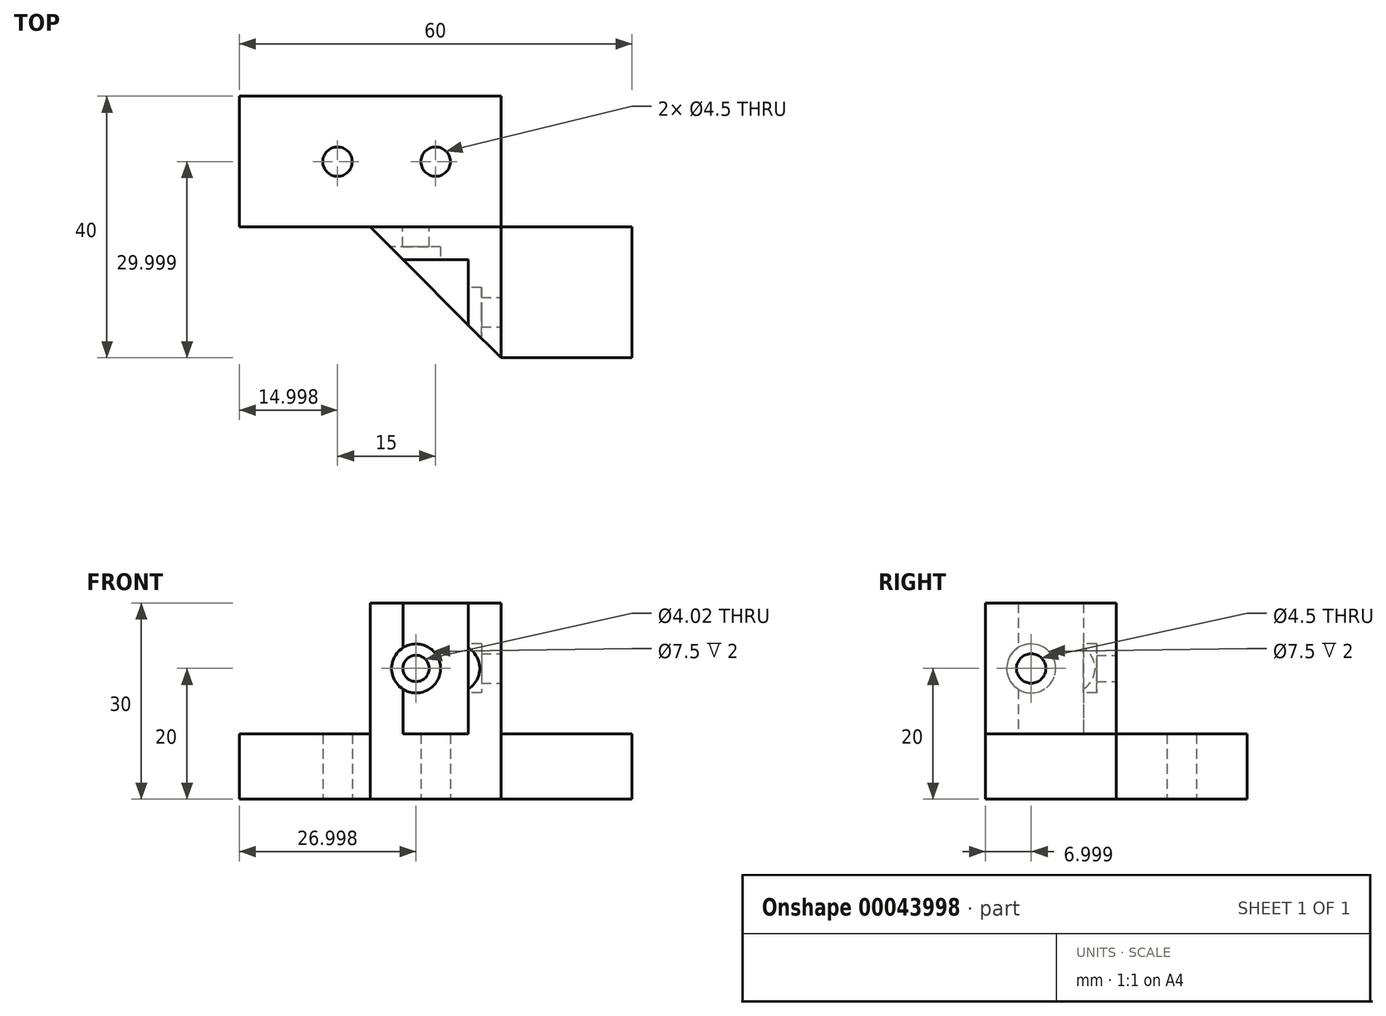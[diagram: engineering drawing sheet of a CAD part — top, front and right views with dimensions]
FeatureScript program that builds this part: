
annotation { "Feature Type Name" : "Feature", "Feature Type Description" : "" }
export const myFeature = defineFeature(function(context is Context, id is Id, definition is map)
    precondition{}
    {
        {
            var Q0;
            Q0=qCreatedBy(makeId("Top.planeOp"),FACE);
            var sketch = newSketch(context, id + "F0", { "sketchPlane" : qUnion([Q0])});
            skLineSegment(sketch, "E0", {"start": v(28.66, -1.44) * mm, "end": v(48.66, -1.44) * mm});
            skLineSegment(sketch, "E1", {"start": v(28.66, 18.56) * mm, "end": v(68.66, 18.56) * mm});
            skLineSegment(sketch, "E2", {"start": v(68.66, 18.56) * mm, "end": v(68.66, -1.44) * mm});
            skLineSegment(sketch, "E3", {"start": v(68.66, -1.44) * mm, "end": v(88.66, -1.44) * mm});
            skLineSegment(sketch, "E4", {"start": v(88.66, -1.44) * mm, "end": v(88.66, -21.44) * mm});
            skLineSegment(sketch, "E5", {"start": v(28.66, 18.56) * mm, "end": v(28.66, -1.44) * mm});
            skLineSegment(sketch, "E6", {"start": v(68.66, 8.56) * mm, "end": v(58.66, 8.56) * mm, "construction": true});
            skCircle(sketch, "E7", {"center": v(58.66, 8.56) * mm, "radius": 2.25 * mm});
            skLineSegment(sketch, "E8", {"start": v(58.66, 8.56) * mm, "end": v(43.66, 8.56) * mm, "construction": true});
            skCircle(sketch, "E9", {"center": v(43.66, 8.56) * mm, "radius": 2.25 * mm});
            skLineSegment(sketch, "E10", {"start": v(68.66, -1.44) * mm, "end": v(68.66, -21.44) * mm, "construction": true});
            skLineSegment(sketch, "E11", {"start": v(48.66, -1.44) * mm, "end": v(68.66, -21.44) * mm});
            skLineSegment(sketch, "E12", {"start": v(68.66, -21.44) * mm, "end": v(88.66, -21.44) * mm});
            skSolve(sketch);
        }
        {
            var Q0;
            Q0 = qSketchRegion(id + "F0", true);
            extrude(context, id + "F1", {"entities" : qUnion([Q0]), "depth" : 10 * mm});
        }
        {
            var Q0;
            Q0=makeQuery(id+"F1.opExtrude","CAP_FACE",FACE,{"disambiguationData":[OSD([sQuery(id+"F0.wireOp",EDGE,"E0"),sQuery(id+"F0.wireOp",EDGE,"E1"),sQuery(id+"F0.wireOp",EDGE,"E2"),sQuery(id+"F0.wireOp",EDGE,"E3"),sQuery(id+"F0.wireOp",EDGE,"E4"),sQuery(id+"F0.wireOp",EDGE,"4b1f2a8e-3ae9-4424-9610-157fee4c87d8"),sQuery(id+"F0.wireOp",EDGE,"e714508f-2f35-4065-8baa-6855e4032ca8"),sQuery(id+"F0.wireOp",EDGE,"E5"),sQuery(id+"F0.wireOp",EDGE,"E7"),sQuery(id+"F0.wireOp",EDGE,"E9")])],"isStart":false});
            var sketch = newSketch(context, id + "F2", { "sketchPlane" : qUnion([Q0])});
            skLineSegment(sketch, "E13", {"start": v(68.66, -1.44) * mm, "end": v(68.66, -21.44) * mm});
            skLineSegment(sketch, "E14", {"start": v(68.66, -1.44) * mm, "end": v(48.66, -1.44) * mm});
            skLineSegment(sketch, "E15", {"start": v(58.66, -1.44) * mm, "end": v(58.66, -6.44) * mm, "construction": true});
            skPoint(sketch, "E15.endSnap0", {"position": v(58.66, -1.44) * mm});
            skLineSegment(sketch, "E16", {"start": v(68.66, -11.44) * mm, "end": v(63.66, -11.44) * mm, "construction": true});
            skLineSegment(sketch, "E17", {"start": v(63.66, -11.44) * mm, "end": v(63.66, -6.44) * mm});
            skLineSegment(sketch, "E18", {"start": v(63.66, -6.44) * mm, "end": v(58.66, -6.44) * mm});
            skLineSegment(sketch, "E19", {"start": v(58.66, -6.44) * mm, "end": v(53.66, -6.44) * mm});
            skLineSegment(sketch, "E20", {"start": v(53.66, -6.44) * mm, "end": v(48.66, -1.44) * mm});
            skLineSegment(sketch, "E21", {"start": v(63.66, -11.44) * mm, "end": v(63.66, -16.44) * mm});
            skLineSegment(sketch, "E22", {"start": v(63.66, -16.44) * mm, "end": v(68.66, -21.44) * mm});
            skSolve(sketch);
        }
        {
            var Q0;
            Q0 = qSketchRegion(id + "F2", true);
            extrude(context, id + "F3", {"entities" : qUnion([Q0]), "operationType" : NewBodyOperationType.ADD, "depth" : 20 * mm});
        }
        {
            var Q0;
            Q0=makeQuery(id+"F3.opExtrude","SWEPT_FACE",FACE,{"disambiguationData":[OSD([sQuery(id+"F2.wireOp",EDGE,"E13")])]});
            var sketch = newSketch(context, id + "F4", { "sketchPlane" : qUnion([Q0])});
            skCircle(sketch, "E23", {"center": v(-14.44, 20) * mm, "radius": 2.25 * mm});
            skSolve(sketch);
        }
        {
            var Q0;
            Q0 = qSketchRegion(id + "F4", true);
            extrude(context, id + "F5", {"entities" : qUnion([Q0]), "operationType" : NewBodyOperationType.REMOVE, "oppositeDirection" : true, "depth" : 5 * mm});
        }
        {
            var Q0;
            Q0=makeQuery(id+"F3.opExtrude","SWEPT_FACE",FACE,{"disambiguationData":[OSD([sQuery(id+"F2.wireOp",EDGE,"E14")])]});
            var sketch = newSketch(context, id + "F6", { "sketchPlane" : qUnion([Q0])});
            skCircle(sketch, "E24", {"center": v(-55.66, 20) * mm, "radius": 2 * mm});
            skSolve(sketch);
        }
        {
            var Q0;
            Q0 = qSketchRegion(id + "F6", true);
            extrude(context, id + "F7", {"entities" : qUnion([Q0]), "operationType" : NewBodyOperationType.REMOVE, "oppositeDirection" : true, "depth" : 5 * mm});
        }
        {
            var Q0;
            Q0=makeQuery(id+"F3.opExtrude","SWEPT_FACE",FACE,{"disambiguationData":[OSD([sQuery(id+"F2.wireOp",EDGE,"E17"),sQuery(id+"F2.wireOp",EDGE,"E21")])]});
            var sketch = newSketch(context, id + "F8", { "sketchPlane" : qUnion([Q0])});
            skCircle(sketch, "E25", {"center": v(14.44, 20) * mm, "radius": 3.75 * mm});
            skSolve(sketch);
        }
        {
            var Q0;
            Q0 = qSketchRegion(id + "F8", true);
            extrude(context, id + "F9", {"entities" : qUnion([Q0]), "operationType" : NewBodyOperationType.REMOVE, "oppositeDirection" : true, "depth" : 2 * mm});
        }
        {
            var Q0;
            Q0=makeQuery(id+"F3.opExtrude","SWEPT_FACE",FACE,{"disambiguationData":[OSD([sQuery(id+"F2.wireOp",EDGE,"E18"),sQuery(id+"F2.wireOp",EDGE,"E19")])]});
            var sketch = newSketch(context, id + "F10", { "sketchPlane" : qUnion([Q0])});
            skCircle(sketch, "E26", {"center": v(55.66, 20) * mm, "radius": 3.75 * mm});
            skSolve(sketch);
        }
        {
            var Q0;
            Q0 = qSketchRegion(id + "F10", true);
            extrude(context, id + "F11", {"entities" : qUnion([Q0]), "operationType" : NewBodyOperationType.REMOVE, "oppositeDirection" : true, "depth" : 2 * mm});
        }
    });
